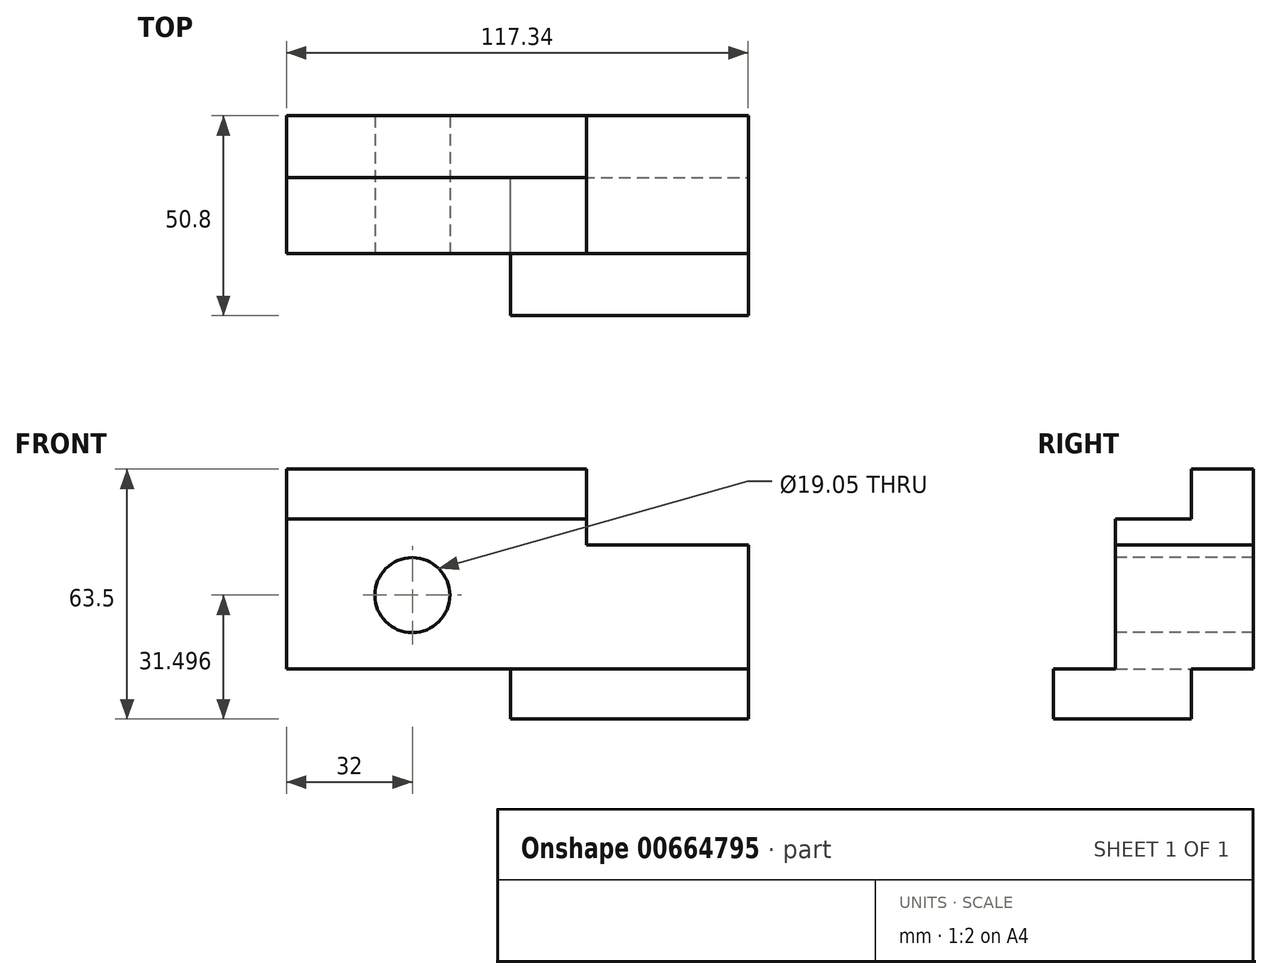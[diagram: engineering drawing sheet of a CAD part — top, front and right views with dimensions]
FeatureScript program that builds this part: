
annotation { "Feature Type Name" : "Feature", "Feature Type Description" : "" }
export const myFeature = defineFeature(function(context is Context, id is Id, definition is map)
    precondition{}
    {
        {
            var Q0;
            Q0=qCreatedBy(makeId("Front.planeOp"),FACE);
            var sketch = newSketch(context, id + "F0", { "sketchPlane" : qUnion([Q0])});
            skLineSegment(sketch, "E0.bottom", {"start": v(58.67, 31.75) * mm, "end": v(-58.67, 31.75) * mm});
            skLineSegment(sketch, "E0.top", {"start": v(58.67, -31.75) * mm, "end": v(-58.67, -31.75) * mm});
            skLineSegment(sketch, "E0.left", {"start": v(58.67, 31.75) * mm, "end": v(58.67, -31.75) * mm});
            skLineSegment(sketch, "E0.right", {"start": v(-58.67, 31.75) * mm, "end": v(-58.67, -31.75) * mm});
            skPoint(sketch, "E0.middle", {"position": v(0, 0) * mm});
            skSolve(sketch);
        }
        {
            var Q0;
            Q0=makeQuery(id+"F0.imprint","IMPRINT",FACE,{"disambiguationData":[TD([[makeQuery(id+"F0.imprint","IMPRINT",EDGE,{"derivedFrom":sQuery(id+"F0.wireOp",EDGE,"E0.bottom")}),1.0]])]});
            extrude(context, id + "F1", {"entities" : qUnion([Q0]), "depth" : 50.8 * mm, "offsetDistance" : 25.4 * mm});
        }
        {
            var Q0;
            Q0=qCreatedBy(makeId("Front.planeOp"),FACE);
            var sketch = newSketch(context, id + "F2", { "sketchPlane" : qUnion([Q0])});
            skLineSegment(sketch, "E1.bottom", {"start": v(17.53, 31.75) * mm, "end": v(58.67, 31.75) * mm});
            skLineSegment(sketch, "E1.top", {"start": v(17.53, 12.45) * mm, "end": v(58.67, 12.45) * mm});
            skLineSegment(sketch, "E1.left", {"start": v(17.53, 31.75) * mm, "end": v(17.53, 12.45) * mm});
            skLineSegment(sketch, "E1.right", {"start": v(58.67, 31.75) * mm, "end": v(58.67, 12.45) * mm});
            skSolve(sketch);
        }
        {
            var Q0;
            Q0=makeQuery(id+"F2.imprint","IMPRINT",FACE,{"disambiguationData":[TD([[makeQuery(id+"F2.imprint","IMPRINT",EDGE,{"derivedFrom":sQuery(id+"F2.wireOp",EDGE,"E1.bottom")}),-1.0]])]});
            extrude(context, id + "F3", {"entities" : qUnion([Q0]), "operationType" : NewBodyOperationType.REMOVE, "endBound" : BoundingType.THROUGH_ALL, "depth" : 25.4 * mm, "offsetDistance" : 25.4 * mm});
        }
        {
            var Q0;
            Q0=qCreatedBy(makeId("Front.planeOp"),FACE);
            var sketch = newSketch(context, id + "F4", { "sketchPlane" : qUnion([Q0])});
            skLineSegment(sketch, "E2.bottom", {"start": v(-58.67, -31.75) * mm, "end": v(-1.78, -31.75) * mm});
            skLineSegment(sketch, "E2.top", {"start": v(-58.67, -19.05) * mm, "end": v(-1.78, -19.05) * mm});
            skLineSegment(sketch, "E2.left", {"start": v(-58.67, -31.75) * mm, "end": v(-58.67, -19.05) * mm});
            skLineSegment(sketch, "E2.right", {"start": v(-1.78, -31.75) * mm, "end": v(-1.78, -19.05) * mm});
            skSolve(sketch);
        }
        {
            var Q0;
            Q0=makeQuery(id+"F4.imprint","IMPRINT",FACE,{"disambiguationData":[TD([[makeQuery(id+"F4.imprint","IMPRINT",EDGE,{"derivedFrom":sQuery(id+"F4.wireOp",EDGE,"E2.bottom")}),1.0]])]});
            extrude(context, id + "F5", {"entities" : qUnion([Q0]), "operationType" : NewBodyOperationType.REMOVE, "endBound" : BoundingType.THROUGH_ALL, "depth" : 25.4 * mm, "offsetDistance" : 25.4 * mm});
        }
        {
            var Q0;
            Q0=makeQuery(id+"F1.opExtrude","SWEPT_FACE",FACE,{"disambiguationData":[OSD([sQuery(id+"F0.wireOp",EDGE,"E0.left")])]});
            var sketch = newSketch(context, id + "F6", { "sketchPlane" : qUnion([Q0])});
            skLineSegment(sketch, "E3.bottom", {"start": v(0, -31.75) * mm, "end": v(-15.75, -31.75) * mm});
            skLineSegment(sketch, "E3.top", {"start": v(0, -19.05) * mm, "end": v(-15.75, -19.05) * mm});
            skLineSegment(sketch, "E3.left", {"start": v(0, -31.75) * mm, "end": v(0, -19.05) * mm});
            skLineSegment(sketch, "E3.right", {"start": v(-15.75, -31.75) * mm, "end": v(-15.75, -19.05) * mm});
            skSolve(sketch);
        }
        {
            var Q0;
            Q0=makeQuery(id+"F6.imprint","IMPRINT",FACE,{"disambiguationData":[TD([[makeQuery(id+"F6.imprint","IMPRINT",EDGE,{"derivedFrom":sQuery(id+"F6.wireOp",EDGE,"E3.bottom")}),1.0]])]});
            extrude(context, id + "F7", {"entities" : qUnion([Q0]), "operationType" : NewBodyOperationType.REMOVE, "endBound" : BoundingType.THROUGH_ALL, "oppositeDirection" : true, "depth" : 25.4 * mm, "offsetDistance" : 25.4 * mm});
        }
        {
            var Q0;
            Q0=makeQuery(id+"F1.opExtrude","SWEPT_FACE",FACE,{"disambiguationData":[OSD([sQuery(id+"F0.wireOp",EDGE,"E0.left")])]});
            var sketch = newSketch(context, id + "F8", { "sketchPlane" : qUnion([Q0])});
            skLineSegment(sketch, "E4.bottom", {"start": v(-50.8, -19.05) * mm, "end": v(-35.05, -19.05) * mm});
            skLineSegment(sketch, "E4.top", {"start": v(-50.8, 31.75) * mm, "end": v(-35.05, 31.75) * mm});
            skLineSegment(sketch, "E4.left", {"start": v(-50.8, -19.05) * mm, "end": v(-50.8, 31.75) * mm});
            skLineSegment(sketch, "E4.right", {"start": v(-35.05, -19.05) * mm, "end": v(-35.05, 31.75) * mm});
            skSolve(sketch);
        }
        {
            var Q0;
            {var subQ0=sQuery(id+"F8.wireOp",EDGE,"E4.top");Q0=makeQuery(id+"F8.imprint","IMPRINT",FACE,{"disambiguationData":[TD([[makeQuery(id+"F8.imprint","IMPRINT",EDGE,{"derivedFrom":subQ0}),-1.0]])]});}
            var Q1;
            {var subQ0=sQuery(id+"F8.wireOp",EDGE,"E4.bottom");Q1=makeQuery(id+"F8.imprint","IMPRINT",FACE,{"disambiguationData":[TD([[makeQuery(id+"F8.imprint","IMPRINT",EDGE,{"derivedFrom":subQ0}),1.0]])]});}
            extrude(context, id + "F9", {"entities" : qUnion([Q0, Q1]), "operationType" : NewBodyOperationType.REMOVE, "endBound" : BoundingType.THROUGH_ALL, "oppositeDirection" : true, "depth" : 25.4 * mm, "offsetDistance" : 25.4 * mm});
        }
        {
            var Q0;
            Q0=makeQuery(id+"F3.boolean.opBoolean","COPY",FACE,{"derivedFrom":makeQuery(id+"F3.opExtrude","SWEPT_FACE",FACE,{"disambiguationData":[OSD([sQuery(id+"F2.wireOp",EDGE,"E1.left")])]})});
            var sketch = newSketch(context, id + "F10", { "sketchPlane" : qUnion([Q0])});
            skLineSegment(sketch, "E5.bottom", {"start": v(-15.75, 31.75) * mm, "end": v(-35.05, 31.75) * mm});
            skLineSegment(sketch, "E5.top", {"start": v(-15.75, 19.05) * mm, "end": v(-35.05, 19.05) * mm});
            skLineSegment(sketch, "E5.left", {"start": v(-15.75, 31.75) * mm, "end": v(-15.75, 19.05) * mm});
            skLineSegment(sketch, "E5.right", {"start": v(-35.05, 31.75) * mm, "end": v(-35.05, 19.05) * mm});
            skSolve(sketch);
        }
        {
            var Q0;
            Q0=makeQuery(id+"F10.imprint","IMPRINT",FACE,{"disambiguationData":[TD([[makeQuery(id+"F10.imprint","IMPRINT",EDGE,{"derivedFrom":sQuery(id+"F10.wireOp",EDGE,"E5.bottom")}),-1.0]])]});
            extrude(context, id + "F11", {"entities" : qUnion([Q0]), "operationType" : NewBodyOperationType.REMOVE, "endBound" : BoundingType.THROUGH_ALL, "oppositeDirection" : true, "depth" : 25.4 * mm, "offsetDistance" : 25.4 * mm});
        }
        {
            var Q0;
            Q0=makeQuery(id+"F9.boolean.opBoolean","COPY",FACE,{"derivedFrom":makeQuery(id+"F9.opExtrude","SWEPT_FACE",FACE,{"disambiguationData":[OSD([sQuery(id+"F8.wireOp",EDGE,"E4.right")])]})});
            var sketch = newSketch(context, id + "F12", { "sketchPlane" : qUnion([Q0])});
            skCircle(sketch, "E6", {"center": v(-26.67, -0.25) * mm, "radius": 9.53 * mm});
            skSolve(sketch);
        }
        {
            var Q0;
            Q0=makeQuery(id+"F12.imprint","IMPRINT",FACE,{"disambiguationData":[TD([[makeQuery(id+"F12.imprint","IMPRINT",EDGE,{"derivedFrom":sQuery(id+"F12.wireOp",EDGE,"E6")}),1.0]])]});
            extrude(context, id + "F13", {"entities" : qUnion([Q0]), "operationType" : NewBodyOperationType.REMOVE, "endBound" : BoundingType.THROUGH_ALL, "oppositeDirection" : true, "depth" : 25.4 * mm, "offsetDistance" : 25.4 * mm});
        }
    });
